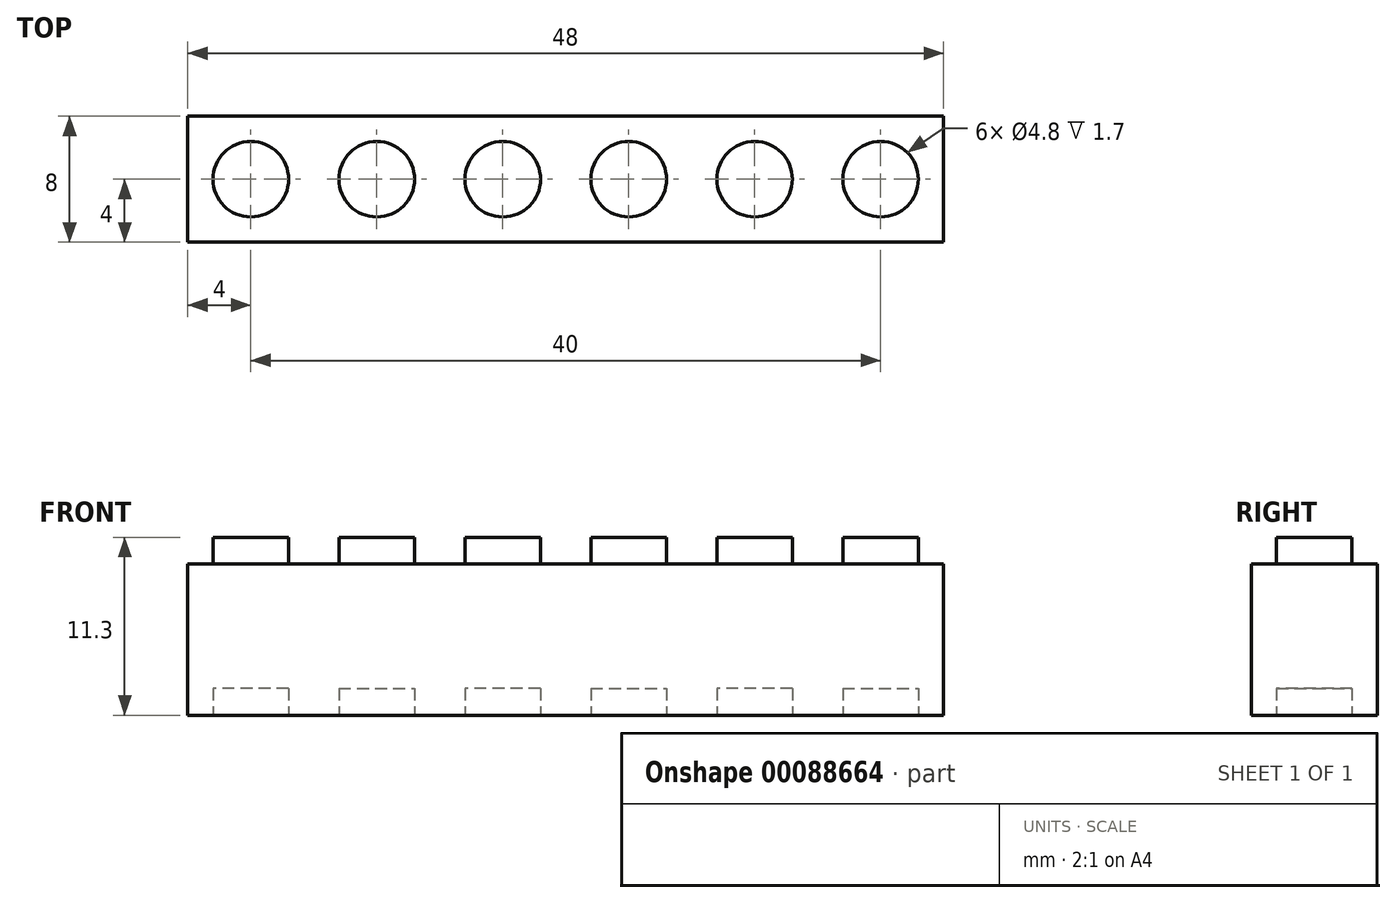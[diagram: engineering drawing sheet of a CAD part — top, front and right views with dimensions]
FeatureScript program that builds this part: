
annotation { "Feature Type Name" : "Feature", "Feature Type Description" : "" }
export const myFeature = defineFeature(function(context is Context, id is Id, definition is map)
    precondition{}
    {
        {
            var Q0;
            Q0=qCreatedBy(makeId("Front.planeOp"),FACE);
            var sketch = newSketch(context, id + "F0", { "sketchPlane" : qUnion([Q0])});
            skLineSegment(sketch, "E0.bottom", {"start": v(-4, 9.6) * mm, "end": v(-2.4, 9.6) * mm});
            skLineSegment(sketch, "E0.top", {"start": v(-4, 0) * mm, "end": v(4, 0) * mm});
            skLineSegment(sketch, "E0.left", {"start": v(-4, 9.6) * mm, "end": v(-4, 0) * mm});
            skLineSegment(sketch, "E0.right", {"start": v(4, 9.6) * mm, "end": v(4, 0) * mm});
            skLineSegment(sketch, "E1.top", {"start": v(-2.4, 11.3) * mm, "end": v(2.4, 11.3) * mm});
            skLineSegment(sketch, "E1.left", {"start": v(-2.4, 9.6) * mm, "end": v(-2.4, 11.3) * mm});
            skLineSegment(sketch, "E1.right", {"start": v(2.4, 9.6) * mm, "end": v(2.4, 11.3) * mm});
            skLineSegment(sketch, "E2", {"start": v(0, 0) * mm, "end": v(0, 24.04) * mm, "construction": true});
            skLineSegment(sketch, "E3.trimOffspring", {"start": v(2.4, 9.6) * mm, "end": v(4, 9.6) * mm});
            skSolve(sketch);
        }
        {
            var Q0;
            Q0=makeQuery(id+"F0.imprint","IMPRINT",FACE,{"disambiguationData":[TD([[makeQuery(id+"F0.imprint","IMPRINT",EDGE,{"derivedFrom":sQuery(id+"F0.wireOp",EDGE,"E0.bottom")}),-1.0]])]});
            extrude(context, id + "F1", {"entities" : qUnion([Q0]), "depth" : 8 * mm});
        }
        {
            var Q0;
            Q0=qCreatedBy(makeId("Top.planeOp"),FACE);
            var Q1;
            Q1=makeQuery(id+"F1.opExtrude","CAP_VERTEX",VERTEX,{"disambiguationData":[OSD([sQuery(id+"F0.wireOp",EDGE,"E1.top"),sQuery(id+"F0.wireOp",EDGE,"E1.right")])],"isStart":true});
            cPlane(context, id + "F2", {"entities" : qUnion([Q0, Q1]), "cplaneType" : CPlaneType.PLANE_POINT, "offset" : 152.4 * mm, "width" : 152.4 * mm, "height" : 152.4 * mm});
        }
        {
            var Q0;
            Q0=qCreatedBy(id+"F2.planeOp",FACE);
            var sketch = newSketch(context, id + "F3", { "sketchPlane" : qUnion([Q0])});
            skLineSegment(sketch, "E4.0", {"start": v(-4, -8) * mm, "end": v(-4, 0) * mm});
            skLineSegment(sketch, "E5.0", {"start": v(4, -8) * mm, "end": v(4, 0) * mm});
            skLineSegment(sketch, "E6", {"start": v(-4, 0) * mm, "end": v(4, 0) * mm});
            skLineSegment(sketch, "E7", {"start": v(-4, -8) * mm, "end": v(4, -8) * mm});
            skLineSegment(sketch, "E8", {"start": v(-4, 0) * mm, "end": v(4, -8) * mm, "construction": true});
            skLineSegment(sketch, "E9", {"start": v(-4, -8) * mm, "end": v(4, 0) * mm, "construction": true});
            skCircle(sketch, "E10", {"center": v(0, -4) * mm, "radius": 2.4 * mm});
            skSolve(sketch);
        }
        {
            var Q0;
            Q0=qSketchRegion(id+"F3",true);
            var Q1;
            Q1=makeQuery(id+"F1.opExtrude","SWEPT_FACE",FACE,{"disambiguationData":[OSD([sQuery(id+"F0.wireOp",EDGE,"E0.bottom")])]});
            extrude(context, id + "F4", {"entities" : qUnion([Q0]), "operationType" : NewBodyOperationType.REMOVE, "endBound" : BoundingType.UP_TO_SURFACE, "oppositeDirection" : true, "endBoundEntityFace" : qUnion([Q1]), "depth" : 25.4 * mm});
        }
        {
            var Q0;
            Q0=qCreatedBy(makeId("Top.planeOp"),FACE);
            var sketch = newSketch(context, id + "F5", { "sketchPlane" : qUnion([Q0])});
            skCircle(sketch, "E11.0", {"center": v(0, -4) * mm, "radius": 2.4 * mm});
            skSolve(sketch);
        }
        {
            var Q0;
            Q0=makeQuery(id+"F5.imprint","IMPRINT",FACE,{"disambiguationData":[TD([[makeQuery(id+"F5.imprint","IMPRINT",EDGE,{"derivedFrom":sQuery(id+"F5.wireOp",EDGE,"E11.0")}),1.0]])]});
            extrude(context, id + "F6", {"entities" : qUnion([Q0]), "operationType" : NewBodyOperationType.REMOVE, "depth" : 1.7 * mm});
        }
        {
            var Q0;
            Q0=qCreatedBy(makeId("Right.planeOp"),FACE);
            var Q1;
            Q1=makeQuery(id+"F1.opExtrude","CAP_VERTEX",VERTEX,{"disambiguationData":[OSD([sQuery(id+"F0.wireOp",EDGE,"E0.right"),sQuery(id+"F0.wireOp",EDGE,"E3.trimOffspring")])],"isStart":false});
            cPlane(context, id + "F7", {"entities" : qUnion([Q0, Q1]), "cplaneType" : CPlaneType.PLANE_POINT, "offset" : 152.4 * mm, "width" : 152.4 * mm, "height" : 152.4 * mm});
        }
        {
            var Q0;
            Q0=makeQuery(id+"F1.opExtrude","SWEPT_BODY",BODY,{"disambiguationData":[OSD([sQuery(id+"F0.wireOp",EDGE,"E0.bottom"),sQuery(id+"F0.wireOp",EDGE,"E0.top"),sQuery(id+"F0.wireOp",EDGE,"E0.left"),sQuery(id+"F0.wireOp",EDGE,"E0.right"),sQuery(id+"F0.wireOp",EDGE,"E1.top"),sQuery(id+"F0.wireOp",EDGE,"E1.left"),sQuery(id+"F0.wireOp",EDGE,"E1.right"),sQuery(id+"F0.wireOp",EDGE,"E3.trimOffspring")])]});
            var Q1;
            Q1=qCreatedBy(id+"F7.planeOp",FACE);
            mirror(context, id + "F8", {"operationType" : NewBodyOperationType.ADD, "entities" : qUnion([Q0]), "mirrorPlane" : qUnion([Q1])});
        }
        {
            var Q0;
            Q0=qCreatedBy(id+"F7.planeOp",FACE);
            var Q1;
            Q1=makeQuery(id+"F8.opPattern","COPY",VERTEX,{"derivedFrom":makeQuery(id+"F1.opExtrude","CAP_VERTEX",VERTEX,{"disambiguationData":[OSD([sQuery(id+"F0.wireOp",EDGE,"E0.bottom"),sQuery(id+"F0.wireOp",EDGE,"E0.left")])],"isStart":false}),"instanceName":"1"});
            cPlane(context, id + "F9", {"entities" : qUnion([Q0, Q1]), "cplaneType" : CPlaneType.PLANE_POINT, "offset" : 152.4 * mm, "width" : 152.4 * mm, "height" : 152.4 * mm});
        }
        {
            var Q0;
            Q0=makeQuery(id+"F1.opExtrude","SWEPT_BODY",BODY,{"disambiguationData":[OSD([sQuery(id+"F0.wireOp",EDGE,"E0.bottom"),sQuery(id+"F0.wireOp",EDGE,"E0.top"),sQuery(id+"F0.wireOp",EDGE,"E0.left"),sQuery(id+"F0.wireOp",EDGE,"E0.right"),sQuery(id+"F0.wireOp",EDGE,"E1.top"),sQuery(id+"F0.wireOp",EDGE,"E1.left"),sQuery(id+"F0.wireOp",EDGE,"E1.right"),sQuery(id+"F0.wireOp",EDGE,"E3.trimOffspring")])]});
            var Q1;
            Q1=qCreatedBy(id+"F9.planeOp",FACE);
            mirror(context, id + "F10", {"operationType" : NewBodyOperationType.ADD, "entities" : qUnion([Q0]), "mirrorPlane" : qUnion([Q1])});
        }
        {
            var Q0;
            Q0=qCreatedBy(makeId("Right.planeOp"),FACE);
            var Q1;
            Q1=makeQuery(id+"F10.opPattern","COPY",VERTEX,{"derivedFrom":makeQuery(id+"F1.opExtrude","CAP_VERTEX",VERTEX,{"disambiguationData":[OSD([sQuery(id+"F0.wireOp",EDGE,"E0.bottom"),sQuery(id+"F0.wireOp",EDGE,"E0.left")])],"isStart":false}),"instanceName":"1"});
            cPlane(context, id + "F11", {"entities" : qUnion([Q0, Q1]), "cplaneType" : CPlaneType.PLANE_POINT, "offset" : 152.4 * mm, "width" : 152.4 * mm, "height" : 152.4 * mm});
        }
        {
            var Q0;
            Q0=makeQuery(id+"F1.opExtrude","SWEPT_BODY",BODY,{"disambiguationData":[OSD([sQuery(id+"F0.wireOp",EDGE,"E0.bottom"),sQuery(id+"F0.wireOp",EDGE,"E0.top"),sQuery(id+"F0.wireOp",EDGE,"E0.left"),sQuery(id+"F0.wireOp",EDGE,"E0.right"),sQuery(id+"F0.wireOp",EDGE,"E1.top"),sQuery(id+"F0.wireOp",EDGE,"E1.left"),sQuery(id+"F0.wireOp",EDGE,"E1.right"),sQuery(id+"F0.wireOp",EDGE,"E3.trimOffspring")])]});
            var Q1;
            Q1=qCreatedBy(id+"F11.planeOp",FACE);
            mirror(context, id + "F12", {"operationType" : NewBodyOperationType.ADD, "entities" : qUnion([Q0]), "mirrorPlane" : qUnion([Q1])});
        }
        {
            var Q0;
            Q0=makeQuery(id+"F12.opPattern","COPY",FACE,{"derivedFrom":makeQuery(id+"F1.opExtrude","SWEPT_FACE",FACE,{"disambiguationData":[OSD([sQuery(id+"F0.wireOp",EDGE,"E0.left")])]}),"instanceName":"1"});
            var sketch = newSketch(context, id + "F13", { "sketchPlane" : qUnion([Q0])});
            skLineSegment(sketch, "E12.bottom", {"start": v(8.15, 19.7) * mm, "end": v(-14.8, 19.7) * mm});
            skLineSegment(sketch, "E12.top", {"start": v(8.15, -11.36) * mm, "end": v(-14.8, -11.36) * mm});
            skLineSegment(sketch, "E12.left", {"start": v(8.15, 19.7) * mm, "end": v(8.15, -11.36) * mm});
            skLineSegment(sketch, "E12.right", {"start": v(-14.8, 19.7) * mm, "end": v(-14.8, -11.36) * mm});
            skPoint(sketch, "E12.middle", {"position": v(-3.32, 4.16) * mm});
            skSolve(sketch);
        }
        {
            var Q0;
            Q0 = qSketchRegion(id + "F13", true);
            extrude(context, id + "F14", {"entities" : qUnion([Q0]), "operationType" : NewBodyOperationType.REMOVE, "oppositeDirection" : true, "depth" : 16 * mm, "offsetDistance" : 25.4 * mm});
        }
    });
